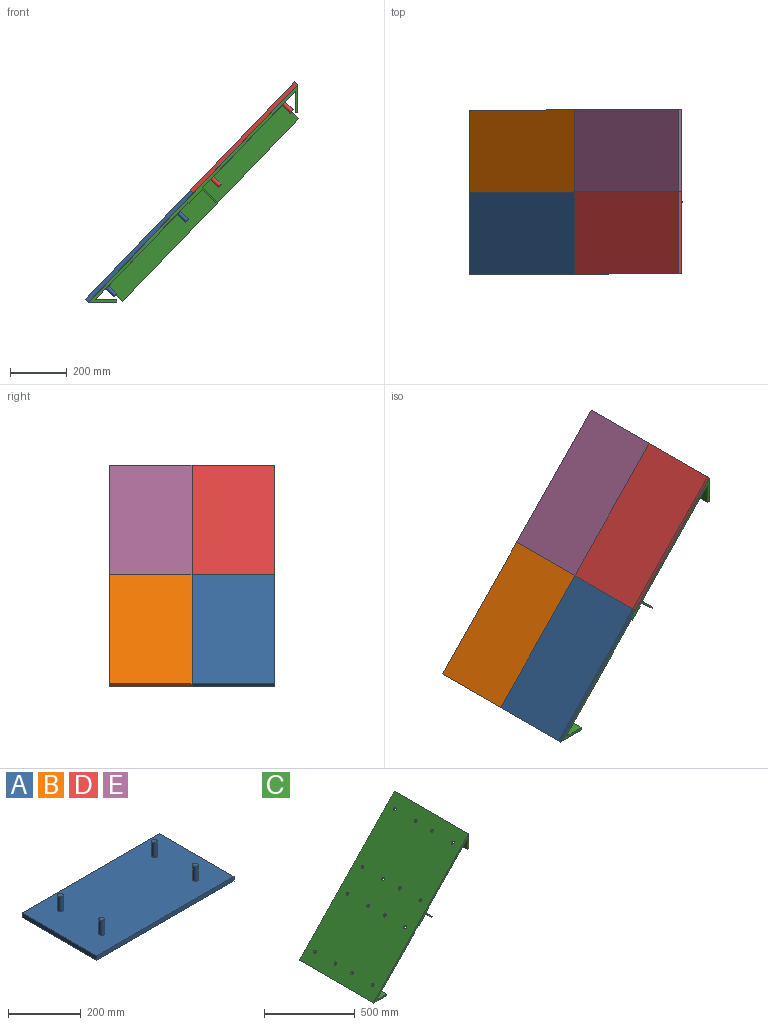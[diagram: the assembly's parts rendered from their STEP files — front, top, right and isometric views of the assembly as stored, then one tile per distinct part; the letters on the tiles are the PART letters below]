
ASSEMBLY  parts=5 mates=4
PART A: 14 faces, bbox 535x290x65 mm
  f0: plane 535x15mm, normal (0,1,0), area 8025mm2, adj f1,f3,f4,f5
  f1: plane 290x15mm, normal (-1,0,0), area 4350mm2, adj f0,f2,f4,f5
  f2: plane 535x15mm, normal (0,-1,0), area 8025mm2, adj f1,f3,f4,f5
  f3: plane 290x15mm, normal (1,0,0), area 4350mm2, adj f0,f2,f4,f5
  f4: plane 535x290mm, normal (0,0,1), area 154345.8mm2, adj f0,f1,f2,f3,f6,f8,f10,f12
  f5: plane 535x290mm, normal (0,0,-1), area 155150mm2, adj f0,f1,f2,f3
  f6: cylinder r=8mm len=50mm, axis (0,0,-1), area 2513.3mm2, adj f4,f7
  f7: plane 16x16mm, normal (0,0,1), area 201.1mm2, adj f6
  f8: cylinder r=8mm len=50mm, axis (0,0,-1), area 2513.3mm2, adj f4,f9
  f9: plane 16x16mm, normal (0,0,1), area 201.1mm2, adj f8
  f10: cylinder r=8mm len=50mm, axis (0,0,-1), area 2513.3mm2, adj f4,f11
  f11: plane 16x16mm, normal (0,0,1), area 201.1mm2, adj f10
  f12: cylinder r=8mm len=50mm, axis (0,0,-1), area 2513.3mm2, adj f4,f13
  f13: plane 16x16mm, normal (0,0,1), area 201.1mm2, adj f12
PART B: same geometry as A
PART C: 69 faces, bbox 743.1x580x770 mm
  f0: plane 580x75.16mm, normal (-1,0,0), area 41717.6mm2, adj f8,f9,f10,f11,f29,f30,f31,f32
  f1: plane 580x100mm, normal (1,0,0), area 56123.1mm2, adj f4,f9,f10,f11,f29,f30,f31,f32
  f2: plane 648.91x623.63mm, normal (0.72,0,-0.69), area 80675mm2, adj f11,f16,f17,f18,f20,f21,f24,f26
  f3: plane 580x341.03mm, normal (0.72,0,-0.69), area 241361.6mm2, adj f7,f10,f11,f14,f15,f16,f17,f18
  f4: plane 770x740mm, normal (-0.72,0,0.69), area 615334.8mm2, adj f1,f5,f10,f11,f53,f54,f55,f56
  f5: plane 580x100mm, normal (0,0,-1), area 54894.1mm2, adj f4,f6,f10,f11,f37,f38,f39,f40
  f6: plane 580x10mm, normal (1,0,0), area 5800mm2, adj f5,f7,f10,f11
  f7: plane 580x76.52mm, normal (0,0,1), area 41275.9mm2, adj f3,f6,f10,f11,f37,f38,f39,f40
  f8: plane 580x340.05mm, normal (0.72,0,-0.69), area 240574.4mm2, adj f0,f10,f11,f12,f13,f19,f20,f21
  f9: plane 580x10mm, normal (0,0,-1), area 5800mm2, adj f0,f1,f10,f11
  f10: plane 770x740mm, normal (0,-1,0), area 12921.3mm2, adj f0,f1,f3,f4,f5,f6,f7,f8
  f11: plane 770x740mm, normal (0,1,0), area 12921.3mm2, adj f0,f1,f2,f3,f4,f5,f6,f7
  f12: plane 349.39x339.91mm, normal (0,-1,0), area 30937.5mm2, adj f8,f13,f21,f25
  f13: plane 252.5x54.08mm, normal (0.69,0,0.72), area 18937.5mm2, adj f8,f10,f12,f25
  f14: plane 252.5x3.61mm, normal (-0.69,0,-0.72), area 1262.5mm2, adj f3,f10,f15,f22
  f15: plane 396.39x388.41mm, normal (0,-1,0), area 35837.5mm2, adj f3,f14,f16,f22,f23,f25
  f16: plane 75x54.08mm, normal (-0.69,0,-0.72), area 725mm2, adj f2,f3,f15,f17,f24,f25
  f17: plane 300.88x289.44mm, normal (0,1,0), area 2062.5mm2, adj f2,f3,f16,f18
  f18: plane 252.5x3.61mm, normal (-0.69,0,-0.72), area 1262.5mm2, adj f2,f3,f11,f17
  f19: plane 252.5x54.08mm, normal (0.69,0,0.72), area 18937.5mm2, adj f8,f11,f20,f26,f28
  f20: plane 300.88x289.44mm, normal (0,1,0), area 2062.5mm2, adj f2,f8,f19,f21
  f21: plane 75x54.08mm, normal (0.69,0,0.72), area 725mm2, adj f2,f8,f12,f20,f24,f25
  f22: plane 252.5x50.47mm, normal (0.72,0,-0.69), area 17675mm2, adj f10,f14,f15,f23
  f23: plane 252.5x50.47mm, normal (-0.69,0,-0.72), area 17675mm2, adj f10,f15,f22,f25
  f24: plane 697.42x674.1mm, normal (0,1,0), area 63000mm2, adj f2,f16,f21,f25
  f25: plane 648.91x623.63mm, normal (0.72,0,-0.69), area 5762.5mm2, adj f10,f12,f13,f15,f16,f21,f23,f24
  f26: plane 53.94x52.11mm, normal (0,-1,0), area 350mm2, adj f2,f19,f27,f28
  f27: plane 252.5x50.47mm, normal (-0.69,0,-0.72), area 17675mm2, adj f2,f11,f26,f28
  f28: plane 252.5x3.61mm, normal (0.72,0,-0.69), area 1262.5mm2, adj f11,f19,f26,f27
  f29: plane 38x10mm, normal (0,-1,0), area 380mm2, adj f0,f1,f30,f31
  f30: cylinder r=9mm len=18mm, axis (1,0,0), area 282.7mm2, adj f0,f1,f29,f32
  f31: cylinder r=9mm len=18mm, axis (1,0,0), area 282.7mm2, adj f0,f1,f29,f32
  f32: plane 38x10mm, normal (0,1,0), area 380mm2, adj f0,f1,f30,f31
  f33: cylinder r=9mm len=18mm, axis (1,0,0), area 282.7mm2, adj f0,f1,f34,f36
  f34: plane 38x10mm, normal (0,1,0), area 380mm2, adj f0,f1,f33,f35
  f35: cylinder r=9mm len=18mm, axis (1,0,0), area 282.7mm2, adj f0,f1,f34,f36
  f36: plane 38x10mm, normal (0,-1,0), area 380mm2, adj f0,f1,f33,f35
  f37: plane 29x10mm, normal (0,1,0), area 290mm2, adj f5,f7,f38,f39
  f38: cylinder r=9mm len=18mm, axis (0,0,-1), area 282.7mm2, adj f5,f7,f37,f40
  f39: cylinder r=9mm len=18mm, axis (0,0,-1), area 282.7mm2, adj f5,f7,f37,f40
  f40: plane 29x10mm, normal (0,-1,0), area 290mm2, adj f5,f7,f38,f39
  f41: plane 29x10mm, normal (0,1,0), area 290mm2, adj f5,f7,f42,f43
  f42: cylinder r=9mm len=18mm, axis (0,0,-1), area 282.7mm2, adj f5,f7,f41,f44
  f43: cylinder r=9mm len=18mm, axis (0,0,-1), area 282.7mm2, adj f5,f7,f41,f44
  f44: plane 29x10mm, normal (0,-1,0), area 290mm2, adj f5,f7,f42,f43
  f45: plane 29x10mm, normal (0,1,0), area 290mm2, adj f5,f7,f46,f47
  f46: cylinder r=9mm len=18mm, axis (0,0,-1), area 282.7mm2, adj f5,f7,f45,f48
  f47: cylinder r=9mm len=18mm, axis (0,0,-1), area 282.7mm2, adj f5,f7,f45,f48
  f48: plane 29x10mm, normal (0,-1,0), area 290mm2, adj f5,f7,f46,f47
  f49: plane 29x10mm, normal (0,1,0), area 290mm2, adj f5,f7,f50,f51
  f50: cylinder r=9mm len=18mm, axis (0,0,-1), area 282.7mm2, adj f5,f7,f49,f52
  f51: cylinder r=9mm len=18mm, axis (0,0,-1), area 282.7mm2, adj f5,f7,f49,f52
  f52: plane 29x10mm, normal (0,-1,0), area 290mm2, adj f5,f7,f50,f51
  f53: cylinder r=9mm len=19.91mm, axis (-0.72,0,0.69), area 565.5mm2, adj f4,f8
  f54: cylinder r=9mm len=19.91mm, axis (-0.72,0,0.69), area 565.5mm2, adj f4,f8
  f55: cylinder r=9mm len=19.91mm, axis (-0.72,0,0.69), area 565.5mm2, adj f4,f8
  f56: cylinder r=9mm len=19.91mm, axis (-0.72,0,0.69), area 565.5mm2, adj f4,f8
  f57: cylinder r=9mm len=19.91mm, axis (-0.72,0,0.69), area 565.5mm2, adj f4,f8
  f58: cylinder r=9mm len=19.91mm, axis (-0.72,0,0.69), area 565.5mm2, adj f4,f8
  f59: cylinder r=9mm len=19.91mm, axis (-0.72,0,0.69), area 565.5mm2, adj f4,f8
  f60: cylinder r=9mm len=19.91mm, axis (-0.72,0,0.69), area 565.5mm2, adj f4,f8
  f61: cylinder r=9mm len=19.91mm, axis (-0.72,0,0.69), area 565.5mm2, adj f3,f4
  f62: cylinder r=9mm len=19.91mm, axis (-0.72,0,0.69), area 565.5mm2, adj f3,f4
  f63: cylinder r=9mm len=19.91mm, axis (-0.72,0,0.69), area 565.5mm2, adj f3,f4
  f64: cylinder r=9mm len=19.91mm, axis (-0.72,0,0.69), area 565.5mm2, adj f3,f4
  f65: cylinder r=9mm len=19.91mm, axis (-0.72,0,0.69), area 565.5mm2, adj f3,f4
  f66: cylinder r=9mm len=19.91mm, axis (-0.72,0,0.69), area 565.5mm2, adj f3,f4
  f67: cylinder r=9mm len=19.91mm, axis (-0.72,0,0.69), area 565.5mm2, adj f3,f4
  f68: cylinder r=9mm len=19.91mm, axis (-0.72,0,0.69), area 565.5mm2, adj f3,f4
PART D: same geometry as A
PART E: same geometry as A
PLACE A rot(axis=(0.92,0,0.39),180deg) t=(34.12,-94.8,-80.49)mm
PLACE B rot(axis=(0.92,0,0.39),180deg) t=(34.12,195.2,-80.49)mm
PLACE C t=(140.25,87.4,8.3)mm
PLACE D rot(axis=(0.92,0,0.39),180deg) t=(404.83,-94.8,305.25)mm
PLACE E rot(axis=(0.92,0,0.39),180deg) t=(404.83,195.2,305.25)mm
MATE fastened A.f8 <-> C.f61  axis (0.72,0,-0.69) through (80.64,22.4,-53.73)mm
MATE fastened D.f6 <-> C.f57  axis (0.72,0,-0.69) through (451.35,-137.6,332.01)mm
MATE fastened B.f6 <-> C.f68  axis (0.72,0,-0.69) through (80.64,152.4,-53.73)mm
MATE fastened E.f6 <-> C.f59  axis (0.72,0,-0.69) through (451.35,152.4,332.01)mm
